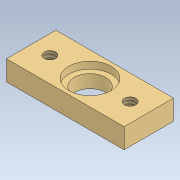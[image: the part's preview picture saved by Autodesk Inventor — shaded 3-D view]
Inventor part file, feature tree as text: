
AUTODESK INVENTOR PART (.ipt)
format: ipt  version: 2022.4 (Build 264492010, 492A)  size: 144,896 bytes
history: native  units: in
note: dims shown in document units (in); Inventor stores cm internally (conversion verified against a paired STEP export)
features: sketch x3, hole x2, other x1, extrude x1
ambient origin geometry x8: Origin, YZ Plane, XZ Plane, XY Plane, X Axis, Y Axis, Z Axis, Center Point
bodies: Solid1 (feature_tree)
feature tree (7):
  other  "main_manifold_8v_v02.ipt"
  sketch  "Sketch:MMC: base"  dims[d8=0.75in d11=0.5635in d12=1.0in d13=0.8108in]
  extrude  "Ex: base"  Depth=0.5635in
  hole  "Hole: flowSensor"  [1 undecoded]
  hole  "Hole: MMC screws"  [1 undecoded]
  sketch  "Sketch:MM: flow sensor"  dims[d37=0.375in d38=0.12in d39=0.5635in d40=0.349in d41=0.8108in]
  sketch  "Sketch:MM: MMC screws"
note: 2 required parameter values undecoded (feature->parameter linkage not recoverable at this tier; creation-order binding heuristic only, values carry confidence <= 0.55)
